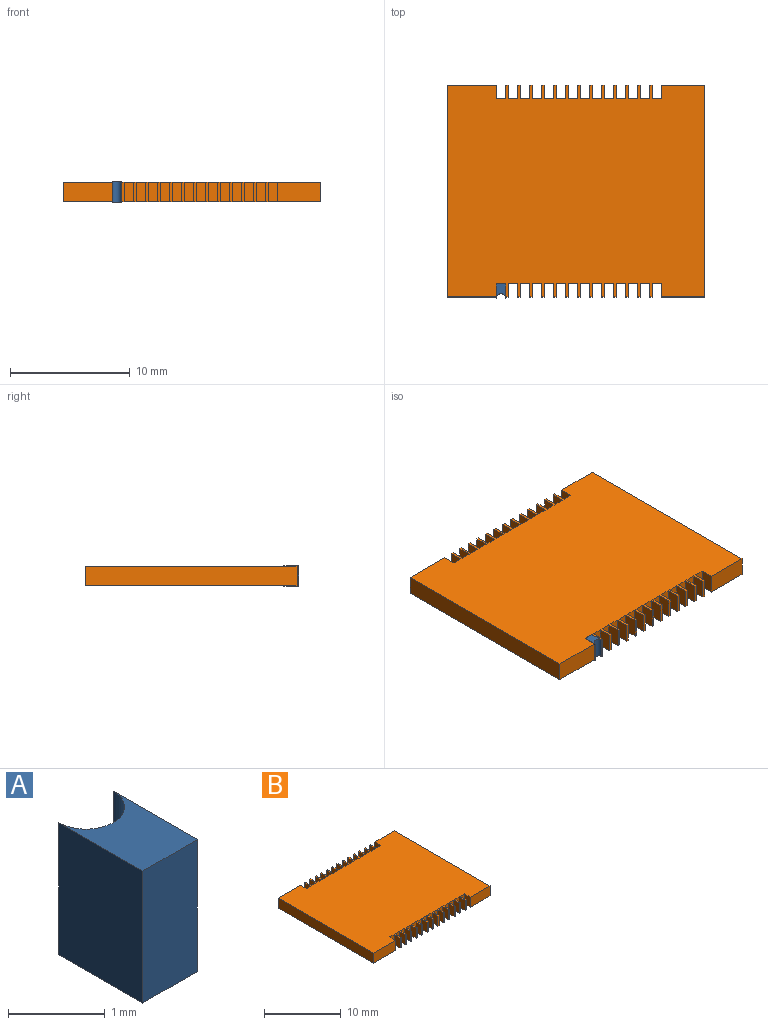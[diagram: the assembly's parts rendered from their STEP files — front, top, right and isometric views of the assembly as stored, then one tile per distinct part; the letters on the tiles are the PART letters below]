
ASSEMBLY  parts=2 mates=1
PART A: 6 faces, bbox 0.8x1.2x1.7 mm
  f0: cylinder r=0.4mm len=1.67mm, axis (0,0,-1), area 2.1mm2, adj f1,f3,f4,f5
  f1: plane 1.67x1.23mm, normal (-1,0,0), area 2.1mm2, adj f0,f2,f4,f5
  f2: plane 1.67x0.8mm, normal (0,-1,0), area 1.3mm2, adj f1,f3,f4,f5
  f3: plane 1.67x1.23mm, normal (1,0,0), area 2.1mm2, adj f0,f2,f4,f5
  f4: plane 1.23x0.8mm, normal (0,0,1), area 0.7mm2, adj f0,f1,f2,f3
  f5: plane 1.23x0.8mm, normal (0,0,-1), area 0.7mm2, adj f0,f1,f2,f3
PART B: 118 faces, bbox 21.5x17.7x1.6 mm
  f0: plane 1.6x0.2mm, normal (0,1,0), area 0.3mm2, adj f28,f29,f91,f116
  f1: plane 1.6x0.2mm, normal (0,1,0), area 0.3mm2, adj f28,f29,f113,f115
  f2: plane 1.6x0.2mm, normal (0,1,0), area 0.3mm2, adj f28,f29,f110,f112
  f3: plane 1.6x0.2mm, normal (0,1,0), area 0.3mm2, adj f28,f29,f107,f109
  f4: plane 1.6x0.2mm, normal (0,1,0), area 0.3mm2, adj f28,f29,f95,f106
  f5: plane 1.6x0.2mm, normal (0,1,0), area 0.3mm2, adj f28,f29,f88,f92
  f6: plane 1.6x0.2mm, normal (0,1,0), area 0.3mm2, adj f28,f29,f85,f89
  f7: plane 1.6x0.2mm, normal (0,1,0), area 0.3mm2, adj f28,f29,f82,f86
  f8: plane 1.6x0.2mm, normal (0,1,0), area 0.3mm2, adj f28,f29,f79,f83
  f9: plane 1.6x0.2mm, normal (0,1,0), area 0.3mm2, adj f28,f29,f76,f80
  f10: plane 1.6x0.2mm, normal (0,1,0), area 0.3mm2, adj f28,f29,f73,f77
  f11: plane 1.6x0.2mm, normal (0,1,0), area 0.3mm2, adj f28,f29,f70,f74
  f12: plane 1.6x0.2mm, normal (0,1,0), area 0.3mm2, adj f28,f29,f36,f71
  f13: plane 4.09x1.6mm, normal (0,1,0), area 6.5mm2, adj f28,f29,f32,f34
  f14: plane 1.6x0.2mm, normal (0,-1,0), area 0.3mm2, adj f28,f29,f41,f104
  f15: plane 1.6x0.2mm, normal (0,-1,0), area 0.3mm2, adj f28,f29,f69,f100
  f16: plane 4.09x1.6mm, normal (0,-1,0), area 6.5mm2, adj f28,f29,f32,f97
  f17: plane 1.6x0.2mm, normal (0,-1,0), area 0.3mm2, adj f28,f29,f54,f68
  f18: plane 1.6x0.2mm, normal (0,-1,0), area 0.3mm2, adj f28,f29,f47,f64
  f19: plane 1.6x0.2mm, normal (0,-1,0), area 0.3mm2, adj f28,f29,f50,f62
  f20: plane 1.6x0.2mm, normal (0,-1,0), area 0.3mm2, adj f28,f29,f39,f58
  f21: plane 1.6x0.2mm, normal (0,-1,0), area 0.3mm2, adj f28,f29,f56,f101
  f22: plane 1.6x0.2mm, normal (0,-1,0), area 0.3mm2, adj f28,f29,f44,f53
  f23: plane 1.6x0.2mm, normal (0,-1,0), area 0.3mm2, adj f28,f29,f49,f65
  f24: plane 1.6x0.2mm, normal (0,-1,0), area 0.3mm2, adj f28,f29,f46,f59
  f25: plane 1.6x0.2mm, normal (0,-1,0), area 0.3mm2, adj f28,f29,f43,f63
  f26: plane 1.6x0.2mm, normal (0,-1,0), area 0.3mm2, adj f28,f29,f40,f57
  f27: plane 1.6x0.2mm, normal (0,-1,0), area 0.3mm2, adj f28,f29,f38,f98
  f28: plane 21.5x17.65mm, normal (0,0,1), area 355mm2, adj f0,f1,f2,f3,f4,f5,f6,f7
  f29: plane 21.5x17.65mm, normal (0,0,-1), area 355mm2, adj f0,f1,f2,f3,f4,f5,f6,f7
  f30: plane 17.65x1.6mm, normal (1,0,0), area 28.2mm2, adj f28,f29,f31,f33
  f31: plane 3.61x1.6mm, normal (0,1,0), area 5.8mm2, adj f28,f29,f30,f94
  f32: plane 17.65x1.6mm, normal (-1,0,0), area 28.2mm2, adj f13,f16,f28,f29
  f33: plane 3.61x1.6mm, normal (0,-1,0), area 5.8mm2, adj f28,f29,f30,f105
  f34: plane 1.6x1.09mm, normal (1,0,0), area 1.7mm2, adj f13,f28,f29,f35
  f35: plane 1.6x0.8mm, normal (0,1,0), area 1.3mm2, adj f28,f29,f34,f36
  f36: plane 1.6x1.09mm, normal (-1,0,0), area 1.7mm2, adj f12,f28,f29,f35
  f37: plane 1.6x0.8mm, normal (0,-1,0), area 1.3mm2, adj f28,f29,f38,f39
  f38: plane 1.6x1.09mm, normal (1,0,0), area 1.7mm2, adj f27,f28,f29,f37
  f39: plane 1.6x1.09mm, normal (-1,0,0), area 1.7mm2, adj f20,f28,f29,f37
  f40: plane 1.6x1.09mm, normal (1,0,0), area 1.7mm2, adj f26,f28,f29,f42
  f41: plane 1.6x1.09mm, normal (-1,0,0), area 1.7mm2, adj f14,f28,f29,f42
  f42: plane 1.6x0.8mm, normal (0,-1,0), area 1.3mm2, adj f28,f29,f40,f41
  f43: plane 1.6x1.09mm, normal (1,0,0), area 1.7mm2, adj f25,f28,f29,f45
  f44: plane 1.6x1.09mm, normal (-1,0,0), area 1.7mm2, adj f22,f28,f29,f45
  f45: plane 1.6x0.8mm, normal (0,-1,0), area 1.3mm2, adj f28,f29,f43,f44
  f46: plane 1.6x1.09mm, normal (1,0,0), area 1.7mm2, adj f24,f28,f29,f48
  f47: plane 1.6x1.09mm, normal (-1,0,0), area 1.7mm2, adj f18,f28,f29,f48
  f48: plane 1.6x0.8mm, normal (0,-1,0), area 1.3mm2, adj f28,f29,f46,f47
  f49: plane 1.6x1.09mm, normal (1,0,0), area 1.7mm2, adj f23,f28,f29,f51
  f50: plane 1.6x1.09mm, normal (-1,0,0), area 1.7mm2, adj f19,f28,f29,f51
  f51: plane 1.6x0.8mm, normal (0,-1,0), area 1.3mm2, adj f28,f29,f49,f50
  f52: plane 1.6x0.8mm, normal (0,-1,0), area 1.3mm2, adj f28,f29,f53,f54
  f53: plane 1.6x1.09mm, normal (1,0,0), area 1.7mm2, adj f22,f28,f29,f52
  f54: plane 1.6x1.09mm, normal (-1,0,0), area 1.7mm2, adj f17,f28,f29,f52
  f55: plane 1.6x0.8mm, normal (0,-1,0), area 1.3mm2, adj f28,f29,f56,f57
  f56: plane 1.6x1.09mm, normal (1,0,0), area 1.7mm2, adj f21,f28,f29,f55
  f57: plane 1.6x1.09mm, normal (-1,0,0), area 1.7mm2, adj f26,f28,f29,f55
  f58: plane 1.6x1.09mm, normal (1,0,0), area 1.7mm2, adj f20,f28,f29,f60
  f59: plane 1.6x1.09mm, normal (-1,0,0), area 1.7mm2, adj f24,f28,f29,f60
  f60: plane 1.6x0.8mm, normal (0,-1,0), area 1.3mm2, adj f28,f29,f58,f59
  f61: plane 1.6x0.8mm, normal (0,-1,0), area 1.3mm2, adj f28,f29,f62,f63
  f62: plane 1.6x1.09mm, normal (1,0,0), area 1.7mm2, adj f19,f28,f29,f61
  f63: plane 1.6x1.09mm, normal (-1,0,0), area 1.7mm2, adj f25,f28,f29,f61
  f64: plane 1.6x1.09mm, normal (1,0,0), area 1.7mm2, adj f18,f28,f29,f66
  f65: plane 1.6x1.09mm, normal (-1,0,0), area 1.7mm2, adj f23,f28,f29,f66
  f66: plane 1.6x0.8mm, normal (0,-1,0), area 1.3mm2, adj f28,f29,f64,f65
  f67: plane 1.6x0.8mm, normal (0,-1,0), area 1.3mm2, adj f28,f29,f68,f69
  f68: plane 1.6x1.09mm, normal (1,0,0), area 1.7mm2, adj f17,f28,f29,f67
  f69: plane 1.6x1.09mm, normal (-1,0,0), area 1.7mm2, adj f15,f28,f29,f67
  f70: plane 1.6x1.09mm, normal (-1,0,0), area 1.7mm2, adj f11,f28,f29,f72
  f71: plane 1.6x1.09mm, normal (1,0,0), area 1.7mm2, adj f12,f28,f29,f72
  f72: plane 1.6x0.8mm, normal (0,1,0), area 1.3mm2, adj f28,f29,f70,f71
  f73: plane 1.6x1.09mm, normal (-1,0,0), area 1.7mm2, adj f10,f28,f29,f75
  f74: plane 1.6x1.09mm, normal (1,0,0), area 1.7mm2, adj f11,f28,f29,f75
  f75: plane 1.6x0.8mm, normal (0,1,0), area 1.3mm2, adj f28,f29,f73,f74
  f76: plane 1.6x1.09mm, normal (-1,0,0), area 1.7mm2, adj f9,f28,f29,f78
  f77: plane 1.6x1.09mm, normal (1,0,0), area 1.7mm2, adj f10,f28,f29,f78
  f78: plane 1.6x0.8mm, normal (0,1,0), area 1.3mm2, adj f28,f29,f76,f77
  f79: plane 1.6x1.09mm, normal (-1,0,0), area 1.7mm2, adj f8,f28,f29,f81
  f80: plane 1.6x1.09mm, normal (1,0,0), area 1.7mm2, adj f9,f28,f29,f81
  f81: plane 1.6x0.8mm, normal (0,1,0), area 1.3mm2, adj f28,f29,f79,f80
  f82: plane 1.6x1.09mm, normal (-1,0,0), area 1.7mm2, adj f7,f28,f29,f84
  f83: plane 1.6x1.09mm, normal (1,0,0), area 1.7mm2, adj f8,f28,f29,f84
  f84: plane 1.6x0.8mm, normal (0,1,0), area 1.3mm2, adj f28,f29,f82,f83
  f85: plane 1.6x1.09mm, normal (-1,0,0), area 1.7mm2, adj f6,f28,f29,f87
  f86: plane 1.6x1.09mm, normal (1,0,0), area 1.7mm2, adj f7,f28,f29,f87
  f87: plane 1.6x0.8mm, normal (0,1,0), area 1.3mm2, adj f28,f29,f85,f86
  f88: plane 1.6x1.09mm, normal (-1,0,0), area 1.7mm2, adj f5,f28,f29,f90
  f89: plane 1.6x1.09mm, normal (1,0,0), area 1.7mm2, adj f6,f28,f29,f90
  f90: plane 1.6x0.8mm, normal (0,1,0), area 1.3mm2, adj f28,f29,f88,f89
  f91: plane 1.6x1.09mm, normal (-1,0,0), area 1.7mm2, adj f0,f28,f29,f93
  f92: plane 1.6x1.09mm, normal (1,0,0), area 1.7mm2, adj f5,f28,f29,f93
  f93: plane 1.6x0.8mm, normal (0,1,0), area 1.3mm2, adj f28,f29,f91,f92
  f94: plane 1.6x1.09mm, normal (-1,0,0), area 1.7mm2, adj f28,f29,f31,f96
  f95: plane 1.6x1.09mm, normal (1,0,0), area 1.7mm2, adj f4,f28,f29,f96
  f96: plane 1.6x0.8mm, normal (0,1,0), area 1.3mm2, adj f28,f29,f94,f95
  f97: plane 1.6x1.09mm, normal (1,0,0), area 1.7mm2, adj f16,f28,f29,f99
  f98: plane 1.6x1.09mm, normal (-1,0,0), area 1.7mm2, adj f27,f28,f29,f99
  f99: plane 1.6x0.8mm, normal (0,-1,0), area 1.3mm2, adj f28,f29,f97,f98
  f100: plane 1.6x1.09mm, normal (1,0,0), area 1.7mm2, adj f15,f28,f29,f102
  f101: plane 1.6x1.09mm, normal (-1,0,0), area 1.7mm2, adj f21,f28,f29,f102
  f102: plane 1.6x0.8mm, normal (0,-1,0), area 1.3mm2, adj f28,f29,f100,f101
  f103: plane 1.6x0.8mm, normal (0,-1,0), area 1.3mm2, adj f28,f29,f104,f105
  f104: plane 1.6x1.09mm, normal (1,0,0), area 1.7mm2, adj f14,f28,f29,f103
  f105: plane 1.6x1.09mm, normal (-1,0,0), area 1.7mm2, adj f28,f29,f33,f103
  f106: plane 1.6x1.09mm, normal (-1,0,0), area 1.7mm2, adj f4,f28,f29,f108
  f107: plane 1.6x1.09mm, normal (1,0,0), area 1.7mm2, adj f3,f28,f29,f108
  f108: plane 1.6x0.8mm, normal (0,1,0), area 1.3mm2, adj f28,f29,f106,f107
  f109: plane 1.6x1.09mm, normal (-1,0,0), area 1.7mm2, adj f3,f28,f29,f111
  f110: plane 1.6x1.09mm, normal (1,0,0), area 1.7mm2, adj f2,f28,f29,f111
  f111: plane 1.6x0.8mm, normal (0,1,0), area 1.3mm2, adj f28,f29,f109,f110
  f112: plane 1.6x1.09mm, normal (-1,0,0), area 1.7mm2, adj f2,f28,f29,f114
  f113: plane 1.6x1.09mm, normal (1,0,0), area 1.7mm2, adj f1,f28,f29,f114
  f114: plane 1.6x0.8mm, normal (0,1,0), area 1.3mm2, adj f28,f29,f112,f113
  f115: plane 1.6x1.09mm, normal (-1,0,0), area 1.7mm2, adj f1,f28,f29,f117
  f116: plane 1.6x1.09mm, normal (1,0,0), area 1.7mm2, adj f0,f28,f29,f117
  f117: plane 1.6x0.8mm, normal (0,1,0), area 1.3mm2, adj f28,f29,f115,f116
PLACE A rot(axis=(0,0,1),180deg) t=(-6.26,-8.35,-0.04)mm
PLACE B at identity fixed
MATE planar A.f2 <-> B.f99  axis (0,1,0) through (-5.86,-7.73,0.8)mm
